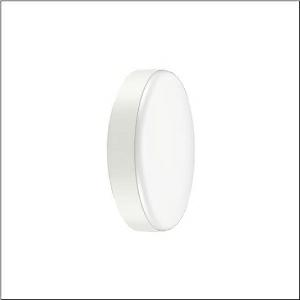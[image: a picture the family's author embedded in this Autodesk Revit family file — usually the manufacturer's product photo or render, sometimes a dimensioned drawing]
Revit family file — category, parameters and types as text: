
# Revit family: rondel_31_51wc10db34as
name_source: partatom
category: Lighting Fixtures
units: mm (PartAtom-declared; Revit-internal decimal feet)

## family parameters
Cut with Voids When Loaded = No
Host = Face
Light Source = No
Part Type = Normal
Room Calculation Point = No
Round Connector Dimension = Use Diameter
Shared = No

## types (1)
- Rondel 31 (1 x LED, 4250 lm, 35.4 W, 3000K)
    Apparent Load = 35 VA
    CIE Flux Codes = 44 75 94 94 100
    Color Rendering = 80
    Color Temperature = 3000K
    Default Elevation = 1800 mm
    Description = Rondel 31, wall and ceiling luminaire, primary optical cover: cover, of PC, opal, light emission: direct distribution, primary light characteristic: symmetric, installation type: surface-mounted, LED, rated luminous flux: 4.100lm, luminous efficacy: 112lm/W, light colour: 830, colour temperature: 3000K, with terminal, 5-pole, max. 2.5mm², mains connection: 220..240V, AC, 50/60Hz, rated input power: 35.5W, luminaire housing, of PC, traffic white (RAL 9016), diameter: 480mm, brightness and presence sensor, HF sensor, protection rating (complete): IP65, insulation class (complete): insulation class II (safety insulation), certification: CE, impact resistance: IK10, permissible storage temperature: -20..+60°C, packaging unit: 1 piece
    Height = 97 mm
    Lamp = 1 x LED
    Lamp Light Flux = 4250 lm
    Lamp Power = 35.4 W
    Lamp count = 1
    Length = 480 mm
    Luminous efficacy = 120 lm/W
    Manufacturer = Siteco
    ModVariant = No
    Model = 51WC10DB34AS
    Mounting Place = Ceiling
    Mounting Type = Surface mounted
    Number of Poles = 1
    OnlyDefault = Yes
    Power Factor = 1
    Product Name = Rondel 31
    Product group = wall and ceiling luminaire
    ProductGroupID = 301
    Protection Class = Protection class II
    Protection Degree = IP 65
    RLX_Detail_Level = 1
    RlxData = <blob elided: 40821 chars, md5=b88afb07>
    Socket = socket
    Standby Power = 0 W
    System Light Flux = 4250 lm
    System Power = 35 W
    Type Comments = Product without accessories
    Type Image = l_1007188.jpg
    URL = http://relux.com
    VarID = ---
    Voltage = 0 V
    Weight = 0.00 kg
    Width = 0 mm  [stored 0 ft]

note: [stored X ft] marks values corroborated as IEEE doubles in the binary element streams (Revit-internal decimal feet)

## geometry (parser evidence)
native form markers: Blend x4, Sweep x12
no freeform markers — native parametric forms only
